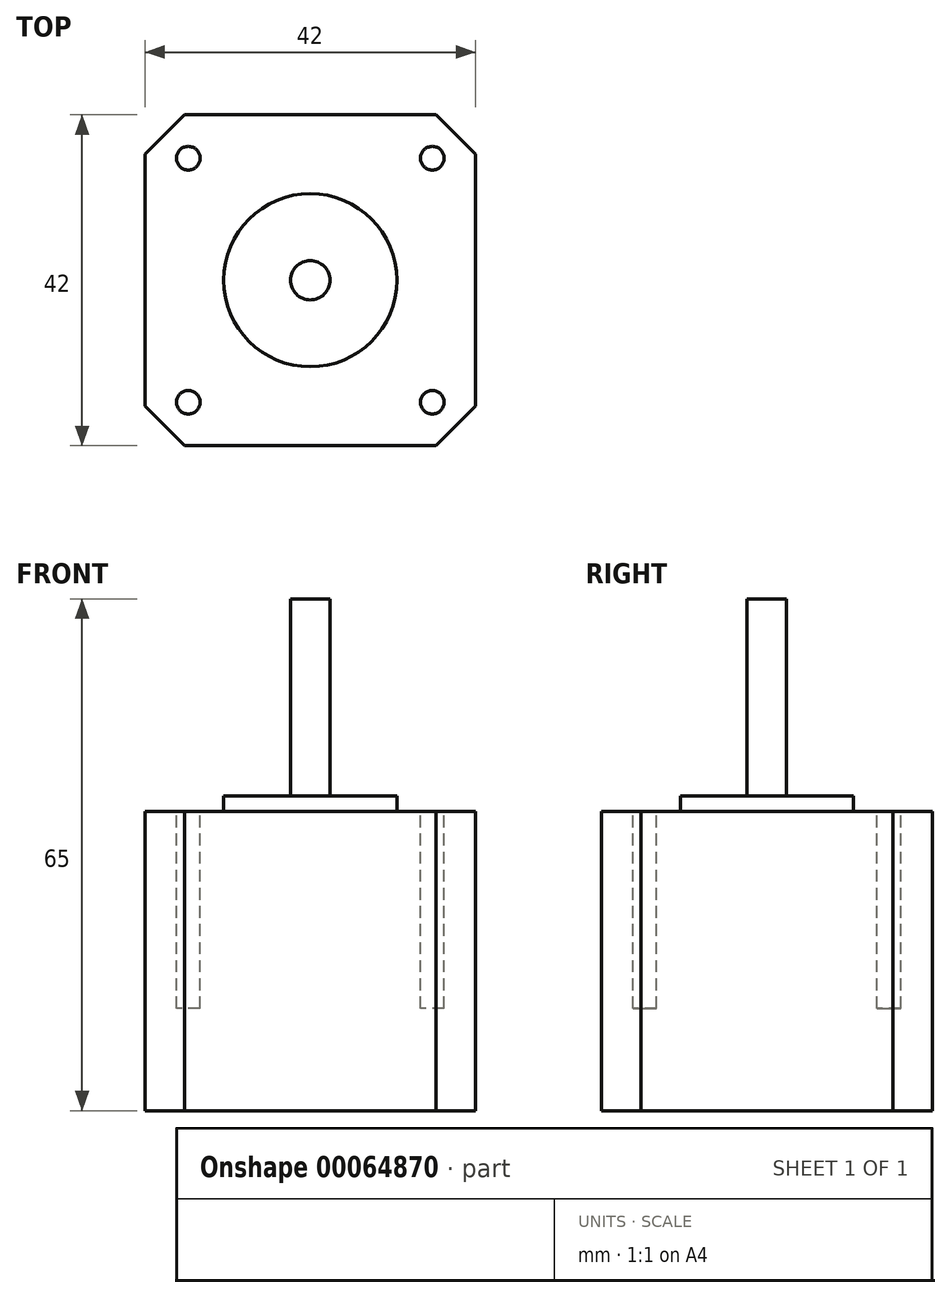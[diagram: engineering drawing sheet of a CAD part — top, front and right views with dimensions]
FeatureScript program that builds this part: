
annotation { "Feature Type Name" : "Feature", "Feature Type Description" : "" }
export const myFeature = defineFeature(function(context is Context, id is Id, definition is map)
    precondition{}
    {
        {
            var Q0;
            Q0=qCreatedBy(makeId("Top.planeOp"),FACE);
            var sketch = newSketch(context, id + "F0", { "sketchPlane" : qUnion([Q0])});
            skLineSegment(sketch, "E0.bottom", {"start": v(0, 0) * mm, "end": v(42, 0) * mm});
            skLineSegment(sketch, "E0.top", {"start": v(0, 42) * mm, "end": v(42, 42) * mm});
            skLineSegment(sketch, "E0.left", {"start": v(0, 0) * mm, "end": v(0, 42) * mm});
            skLineSegment(sketch, "E0.right", {"start": v(42, 0) * mm, "end": v(42, 42) * mm});
            skSolve(sketch);
        }
        {
            var Q0;
            Q0=qSketchRegion(id+"F0",true);
            extrude(context, id + "F1", {"entities" : qUnion([Q0]), "depth" : 38 * mm});
        }
        {
            var Q0;
            Q0=makeQuery(id+"F1.opExtrude","SWEPT_EDGE",EDGE,{"disambiguationData":[OSD([sQuery(id+"F0.wireOp",EDGE,"E0.bottom"),sQuery(id+"F0.wireOp",EDGE,"E0.left")])]});
            var Q1;
            Q1=makeQuery(id+"F1.opExtrude","SWEPT_EDGE",EDGE,{"disambiguationData":[OSD([sQuery(id+"F0.wireOp",EDGE,"E0.top"),sQuery(id+"F0.wireOp",EDGE,"E0.left")])]});
            var Q2;
            Q2=makeQuery(id+"F1.opExtrude","SWEPT_EDGE",EDGE,{"disambiguationData":[OSD([sQuery(id+"F0.wireOp",EDGE,"E0.bottom"),sQuery(id+"F0.wireOp",EDGE,"E0.right")])]});
            var Q3;
            Q3=makeQuery(id+"F1.opExtrude","SWEPT_EDGE",EDGE,{"disambiguationData":[OSD([sQuery(id+"F0.wireOp",EDGE,"E0.top"),sQuery(id+"F0.wireOp",EDGE,"E0.right")])]});
            chamfer(context, id + "F2", {"entities" : qUnion([Q0, Q1, Q2, Q3]), "width" : 5 * mm, "tangentPropagation" : true});
        }
        {
            var Q0;
            Q0=makeQuery(id+"F1.opExtrude","CAP_FACE",FACE,{"disambiguationData":[OSD([sQuery(id+"F0.wireOp",EDGE,"E0.bottom"),sQuery(id+"F0.wireOp",EDGE,"E0.top"),sQuery(id+"F0.wireOp",EDGE,"E0.left"),sQuery(id+"F0.wireOp",EDGE,"E0.right")])],"isStart":false});
            var sketch = newSketch(context, id + "F3", { "sketchPlane" : qUnion([Q0])});
            skCircle(sketch, "E1", {"center": v(21, 21) * mm, "radius": 11 * mm});
            skSolve(sketch);
        }
        {
            var Q0;
            Q0=qSketchRegion(id+"F3",true);
            extrude(context, id + "F4", {"entities" : qUnion([Q0]), "operationType" : NewBodyOperationType.ADD, "depth" : 2 * mm});
        }
        {
            var Q0;
            Q0=makeQuery(id+"F4.opExtrude","CAP_FACE",FACE,{"disambiguationData":[OSD([sQuery(id+"F3.wireOp",EDGE,"E1")])],"isStart":false});
            var sketch = newSketch(context, id + "F5", { "sketchPlane" : qUnion([Q0])});
            skCircle(sketch, "E2", {"center": v(21, 21) * mm, "radius": 2.5 * mm});
            skSolve(sketch);
        }
        {
            var Q0;
            Q0=qSketchRegion(id+"F5",true);
            extrude(context, id + "F6", {"entities" : qUnion([Q0]), "operationType" : NewBodyOperationType.ADD, "depth" : 25 * mm, "offsetDistance" : 25 * mm});
        }
        {
            var Q0;
            Q0=makeQuery(id+"F1.opExtrude","CAP_FACE",FACE,{"disambiguationData":[OSD([sQuery(id+"F0.wireOp",EDGE,"E0.bottom"),sQuery(id+"F0.wireOp",EDGE,"E0.top"),sQuery(id+"F0.wireOp",EDGE,"E0.left"),sQuery(id+"F0.wireOp",EDGE,"E0.right")])],"isStart":false});
            var sketch = newSketch(context, id + "F7", { "sketchPlane" : qUnion([Q0])});
            skCircle(sketch, "E3", {"center": v(5.5, 36.5) * mm, "radius": 1.5 * mm});
            skCircle(sketch, "E4", {"center": v(5.5, 5.5) * mm, "radius": 1.5 * mm});
            skCircle(sketch, "E5", {"center": v(36.5, 36.5) * mm, "radius": 1.5 * mm});
            skCircle(sketch, "E6", {"center": v(36.5, 5.5) * mm, "radius": 1.5 * mm});
            skSolve(sketch);
        }
        {
            var Q0;
            Q0=qSketchRegion(id+"F7",true);
            extrude(context, id + "F8", {"entities" : qUnion([Q0]), "operationType" : NewBodyOperationType.REMOVE, "oppositeDirection" : true, "depth" : 25 * mm});
        }
    });
